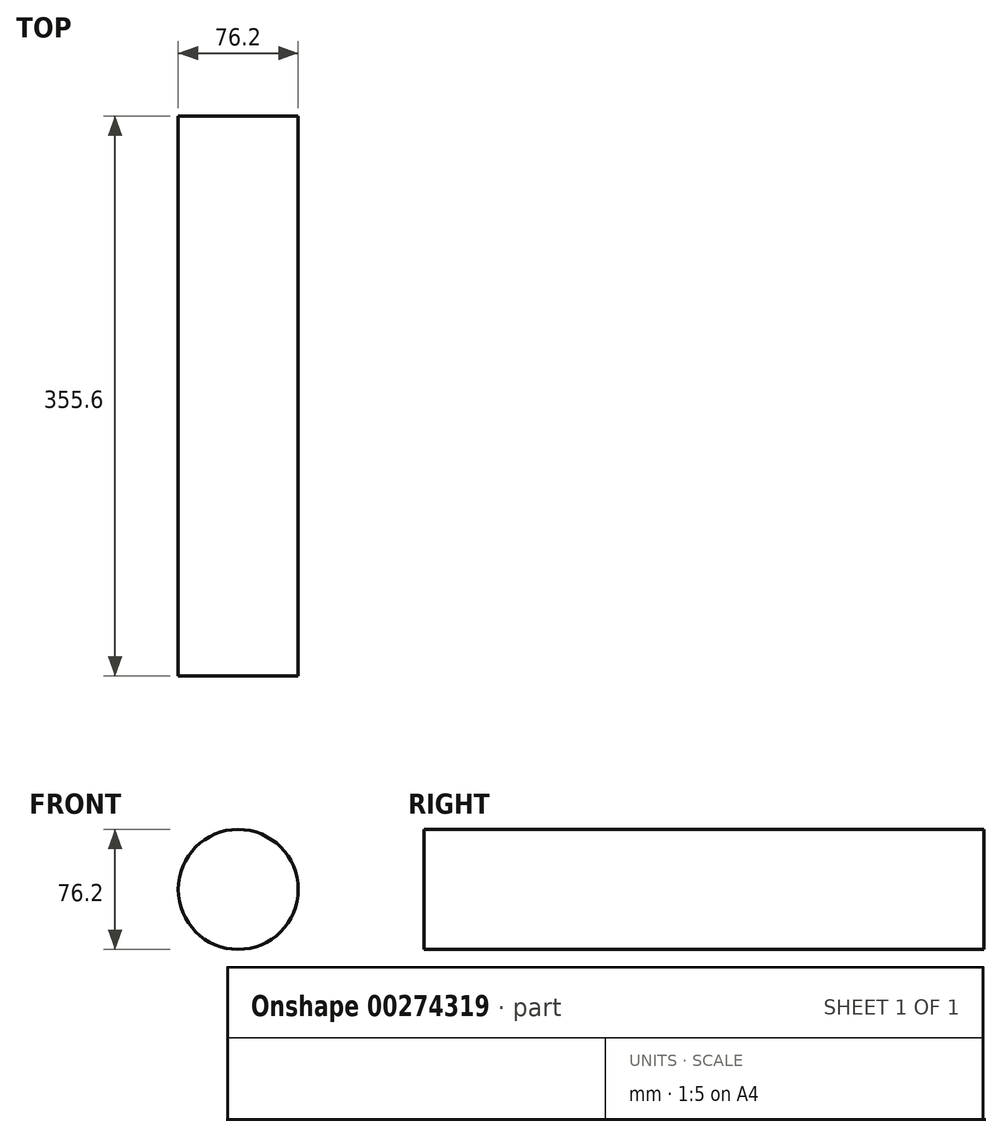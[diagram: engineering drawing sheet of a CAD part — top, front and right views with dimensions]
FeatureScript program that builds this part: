
annotation { "Feature Type Name" : "Feature", "Feature Type Description" : "" }
export const myFeature = defineFeature(function(context is Context, id is Id, definition is map)
    precondition{}
    {
        {
            var Q0;
            Q0=qCreatedBy(makeId("Front.planeOp"),FACE);
            var sketch = newSketch(context, id + "F0", { "sketchPlane" : qUnion([Q0])});
            skCircle(sketch, "E0", {"center": v(0, 0) * mm, "radius": 38.1 * mm});
            skSolve(sketch);
        }
        {
            var Q0;
            Q0 = qSketchRegion(id + "F0", true);
            extrude(context, id + "F1", {"entities" : qUnion([Q0]), "oppositeDirection" : true, "depth" : 355.6 * mm});
        }
    });
